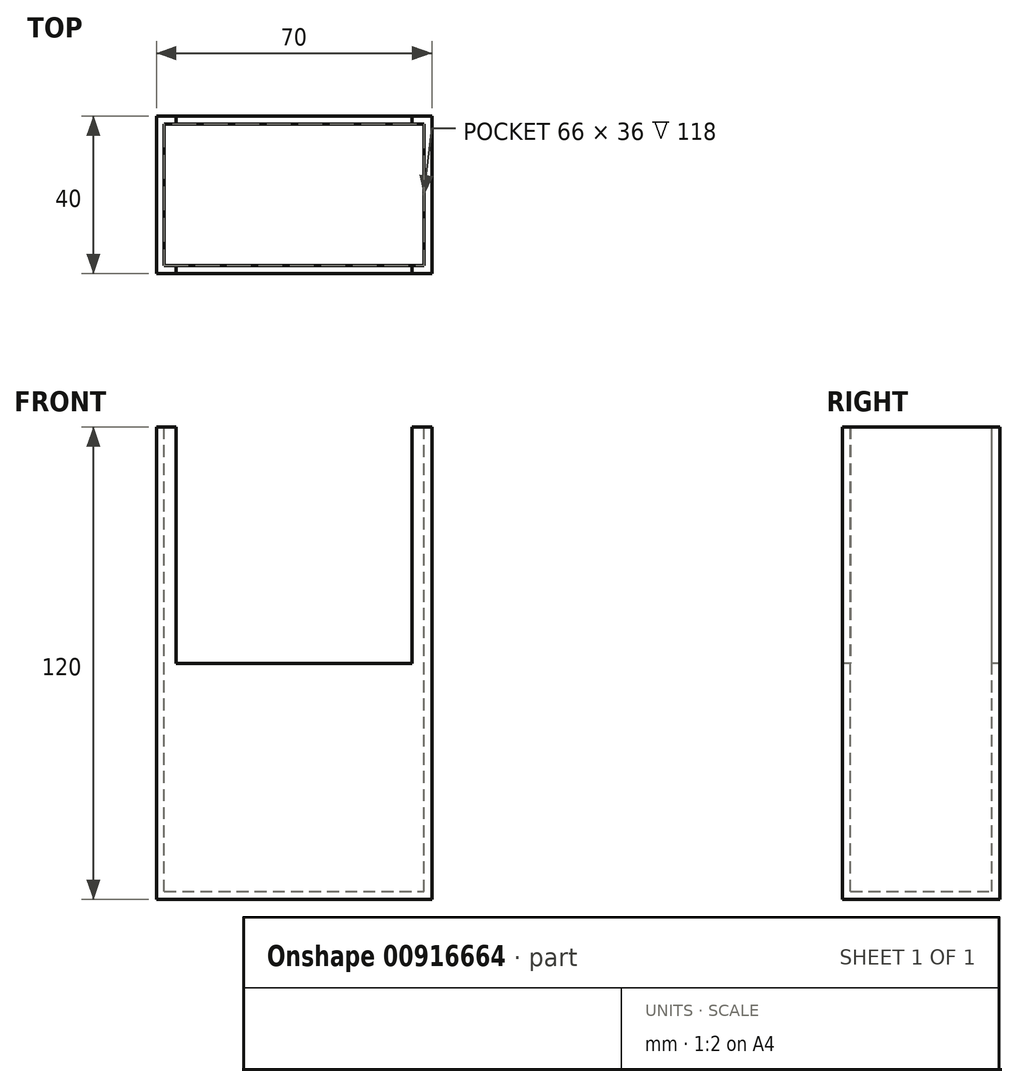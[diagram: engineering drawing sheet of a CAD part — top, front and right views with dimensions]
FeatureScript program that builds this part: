
annotation { "Feature Type Name" : "Feature", "Feature Type Description" : "" }
export const myFeature = defineFeature(function(context is Context, id is Id, definition is map)
    precondition{}
    {
        {
            var Q0;
            Q0=qCreatedBy(makeId("Top.planeOp"),FACE);
            var sketch = newSketch(context, id + "F0", { "sketchPlane" : qUnion([Q0])});
            skLineSegment(sketch, "E0.bottom", {"start": v(0, 0) * mm, "end": v(70, 0) * mm});
            skLineSegment(sketch, "E0.top", {"start": v(0, -40) * mm, "end": v(70, -40) * mm});
            skLineSegment(sketch, "E0.left", {"start": v(0, 0) * mm, "end": v(0, -40) * mm});
            skLineSegment(sketch, "E0.right", {"start": v(70, 0) * mm, "end": v(70, -40) * mm});
            skSolve(sketch);
        }
        {
            var Q0;
            Q0=makeQuery(id+"F0.imprint","IMPRINT",FACE,{"disambiguationData":[TD([[makeQuery(id+"F0.imprint","IMPRINT",EDGE,{"derivedFrom":sQuery(id+"F0.wireOp",EDGE,"E0.bottom")}),-1.0]])]});
            extrude(context, id + "F1", {"entities" : qUnion([Q0]), "depth" : 120 * mm, "offsetDistance" : 25 * mm});
        }
        {
            var Q0;
            Q0=makeQuery(id+"F1.opExtrude","CAP_FACE",FACE,{"disambiguationData":[OSD([sQuery(id+"F0.wireOp",EDGE,"E0.bottom"),sQuery(id+"F0.wireOp",EDGE,"E0.top"),sQuery(id+"F0.wireOp",EDGE,"E0.left"),sQuery(id+"F0.wireOp",EDGE,"E0.right")])],"isStart":false});
            var sketch = newSketch(context, id + "F2", { "sketchPlane" : qUnion([Q0])});
            skLineSegment(sketch, "E1.0", {"start": v(2, -2) * mm, "end": v(2, -38) * mm});
            skLineSegment(sketch, "E1.1", {"start": v(68, -2) * mm, "end": v(2, -2) * mm});
            skLineSegment(sketch, "E1.2", {"start": v(68, -38) * mm, "end": v(68, -2) * mm});
            skLineSegment(sketch, "E1.3", {"start": v(2, -38) * mm, "end": v(68, -38) * mm});
            skSolve(sketch);
        }
        {
            var Q0;
            Q0=makeQuery(id+"F2.imprint","IMPRINT",FACE,{"disambiguationData":[TD([[makeQuery(id+"F2.imprint","IMPRINT",EDGE,{"derivedFrom":sQuery(id+"F2.wireOp",EDGE,"E1.0")}),1.0]])]});
            extrude(context, id + "F3", {"entities" : qUnion([Q0]), "operationType" : NewBodyOperationType.REMOVE, "endBound" : BoundingType.UP_TO_NEXT, "oppositeDirection" : true, "depth" : 25 * mm, "hasOffset" : true, "offsetDistance" : 2 * mm});
        }
        {
            var Q0;
            Q0=makeQuery(id+"F1.opExtrude","SWEPT_FACE",FACE,{"disambiguationData":[OSD([sQuery(id+"F0.wireOp",EDGE,"E0.top")])]});
            var sketch = newSketch(context, id + "F4", { "sketchPlane" : qUnion([Q0])});
            skLineSegment(sketch, "E2.0", {"start": v(5, 120) * mm, "end": v(5, 60) * mm});
            skLineSegment(sketch, "E3.0", {"start": v(65, 120) * mm, "end": v(65, 60) * mm});
            skLineSegment(sketch, "E4.0", {"start": v(5, 60) * mm, "end": v(65, 60) * mm});
            skLineSegment(sketch, "E5.0", {"start": v(-5, -5) * mm, "end": v(75, -5) * mm});
            skLineSegment(sketch, "E5.1", {"start": v(-5, 125) * mm, "end": v(-5, -5) * mm});
            skLineSegment(sketch, "E5.2", {"start": v(75, 125) * mm, "end": v(-5, 125) * mm});
            skLineSegment(sketch, "E5.3", {"start": v(75, -5) * mm, "end": v(75, 125) * mm});
            skSolve(sketch);
        }
        {
            var Q0;
            {var subQ0=sQuery(id+"F4.wireOp",EDGE,"E2.0");Q0=makeQuery(id+"F4.imprint","IMPRINT",FACE,{"disambiguationData":[TD([[makeQuery(id+"F4.imprint","IMPRINT",EDGE,{"derivedFrom":subQ0}),1.0]])]});}
            extrude(context, id + "F5", {"entities" : qUnion([Q0]), "operationType" : NewBodyOperationType.REMOVE, "endBound" : BoundingType.THROUGH_ALL, "oppositeDirection" : true, "depth" : 25 * mm, "offsetDistance" : 25 * mm});
        }
    });
